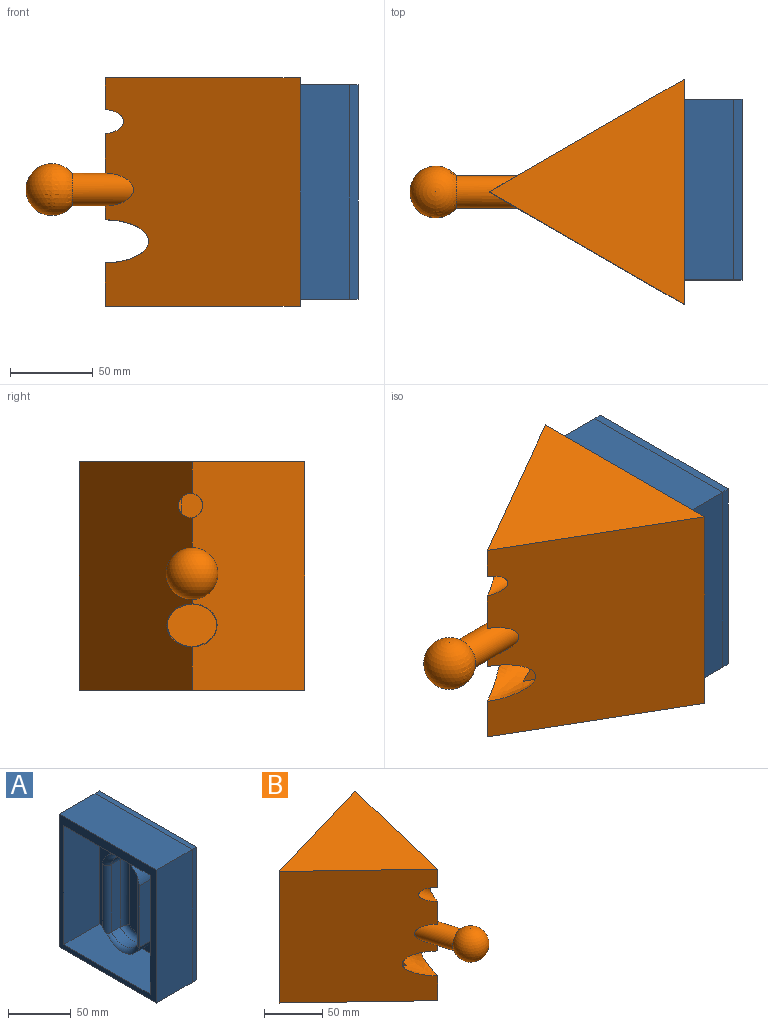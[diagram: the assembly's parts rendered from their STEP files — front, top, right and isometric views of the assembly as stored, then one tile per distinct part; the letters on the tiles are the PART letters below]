
ASSEMBLY  parts=2 mates=1
PART A: 32 faces, bbox 45x109.3x129.5 mm
  f0: plane 115.86x96.9mm, normal (-1,0,0), area 7727.7mm2, adj f6,f7,f8,f9,f15,f16,f17,f18
  f1: plane 129.49x109.26mm, normal (-1,0,0), area 2921.5mm2, adj f2,f3,f4,f5,f6,f7,f8,f9
  f2: plane 109.27x40mm, normal (0,0,1), area 4370.6mm2, adj f1,f3,f5,f10
  f3: plane 129.49x40mm, normal (0,-1,0), area 5179.5mm2, adj f1,f2,f4,f11
  f4: plane 109.29x40.02mm, normal (0,0,-1), area 4370.7mm2, adj f1,f3,f5,f12
  f5: plane 129.5x40.01mm, normal (0,1,0), area 5179.5mm2, adj f1,f2,f4,f13
  f6: plane 115.86x40mm, normal (0,1,0), area 4634.4mm2, adj f0,f1,f7,f9
  f7: plane 96.9x40mm, normal (0,0,1), area 3876mm2, adj f0,f1,f6,f8
  f8: plane 115.86x40mm, normal (0,-1,0), area 4634.4mm2, adj f0,f1,f7,f9
  f9: plane 96.9x40mm, normal (0,0,-1), area 3876mm2, adj f0,f1,f6,f8
  f10: plane 109.27x5mm, normal (0,0,1), area 546.4mm2, adj f2,f11,f13,f14
  f11: plane 129.48x5mm, normal (0,-1,0), area 647.4mm2, adj f3,f10,f12,f14
  f12: plane 109.29x5.02mm, normal (0,0,-1), area 546.4mm2, adj f4,f11,f13,f14
  f13: plane 129.5x5.01mm, normal (0,1,0), area 647.4mm2, adj f5,f10,f12,f14
  f14: plane 129.48x109.27mm, normal (1,0,0), area 14148.2mm2, adj f10,f11,f12,f13
  f15: plane 60x25mm, normal (0,-1,0), area 1500mm2, adj f0,f16,f18,f28
  f16: cylinder r=21mm len=41.56mm, axis (1,0,0), area 1481.5mm2, adj f0,f15,f17,f28,f29,f31
  f17: plane 60x25mm, normal (0,1,0), area 1500mm2, adj f0,f16,f18,f31
  f18: cylinder r=22.1mm len=41.56mm, axis (1,0,0), area 1310.4mm2, adj f0,f15,f17,f28,f30,f31
  f19: cylinder r=17.15mm len=31.56mm, axis (1,0,0), area 416.2mm2, adj f20,f22,f25,f29
  f20: plane 66.05x10mm, normal (0,1,0), area 660.5mm2, adj f19,f21,f24,f28
  f21: cylinder r=19.07mm len=31.56mm, axis (1,0,0), area 381.9mm2, adj f20,f22,f26,f30
  f22: plane 66x10mm, normal (0,-1,0), area 660mm2, adj f19,f21,f27,f31
  f23: plane 76.26x21.56mm, normal (-1,0,0), area 1563.2mm2, adj f24,f25,f26,f27
  f24: cylinder r=5mm len=66.05mm, axis (0,0,-1), area 508.7mm2, adj f20,f23,f25,f26
  f25: torus R=12.15mm, axis (-1,0,0), area 284.4mm2, adj f19,f23,f24,f27
  f26: torus R=14.07mm, axis (-1,0,0), area 258.8mm2, adj f21,f23,f24,f27
  f27: cylinder r=5mm len=66mm, axis (0,0,1), area 508.1mm2, adj f22,f23,f25,f26
  f28: cylinder r=5mm len=67.65mm, axis (0,0,1), area 518.1mm2, adj f15,f16,f18,f20,f29,f30
  f29: torus R=22.15mm, axis (-1,0,0), area 304mm2, adj f16,f19,f28,f31
  f30: torus R=24.07mm, axis (-1,0,0), area 229.5mm2, adj f18,f21,f28,f31
  f31: cylinder r=5mm len=66.89mm, axis (0,0,-1), area 511.9mm2, adj f16,f17,f18,f22,f29,f30
PART B: 22 faces, bbox 130.4x178.8x138 mm
  f0: plane 120x46.13mm, normal (0.76,0.66,0), area 6359.6mm2, adj f13,f14,f15,f16,f17,f20,f21
  f1: plane 138x132.23mm, normal (0.97,-0.23,0), area 17703.2mm2, adj f2,f3,f4,f5,f6,f13,f20
  f2: plane 138x98.6mm, normal (-0.69,-0.73,0), area 17654.1mm2, adj f1,f3,f4,f5,f6,f13,f20
  f3: cylinder r=9.85mm len=41.2mm, axis (-0.28,0.96,0), area 1910.7mm2, adj f1,f2,f12
  f4: plane 138x130.42mm, normal (-0.28,0.96,0), area 4619.9mm2, adj f1,f2,f5,f6,f7,f8,f9,f10
  f5: plane 132.23x130.42mm, normal (0,0,1), area 8009mm2, adj f1,f2,f4
  f6: plane 132.23x130.42mm, normal (0,0,-1), area 8009mm2, adj f1,f2,f4
  f7: plane 107.61x40.57mm, normal (0,0,-1), area 1092.6mm2, adj f4,f8,f10,f11
  f8: plane 129.49x9.59mm, normal (-0.96,-0.28,0), area 1294.9mm2, adj f4,f7,f9,f11
  f9: plane 107.61x40.57mm, normal (0,0,1), area 1092.6mm2, adj f4,f8,f10,f11
  f10: plane 129.49x9.59mm, normal (0.96,0.28,0), area 1294.9mm2, adj f4,f7,f9,f11
  f11: plane 129.49x104.78mm, normal (-0.28,0.96,0), area 14148.1mm2, adj f7,f8,f9,f10
  f12: sphere r=15.68mm, area 2745.9mm2, adj f3
  f13: extruded ~70.04x47.19mm, area 2748.6mm2, adj f0,f1,f2,f14
  f14: plane 120x57.75mm, normal (-0.95,0.33,0), area 6693.2mm2, adj f0,f13,f15,f16,f17,f20
  f15: plane 120x59.97mm, normal (0.19,-0.98,0), area 6710mm2, adj f0,f14,f16,f17,f19
  f16: plane 59.97x57.75mm, normal (0,0,1), area 1616mm2, adj f0,f14,f15
  f17: plane 59.97x57.75mm, normal (0,0,-1), area 1616mm2, adj f0,f14,f15
  f18: plane 29.03x26mm, normal (0.28,-0.96,0), area 618.1mm2, adj f19
  f19: extruded ~34.05x26mm, area 1439mm2, adj f15,f18
  f20: cylinder r=7.28mm len=47.07mm, axis (0.28,-0.96,0), area 1396.9mm2, adj f0,f1,f2,f14,f21
  f21: plane 9.6x1.73mm, normal (0.28,-0.96,0), area 11.9mm2, adj f0,f20
PLACE A t=(256.54,-221.53,212.49)mm
PLACE B rot(axis=(0,0,-1),106.5deg) t=(227.28,-223.58,142.44)mm
MATE fastened B.f11 <-> A.f1  axis (1,0,0) through (256.54,-167.53,276.18)mm
